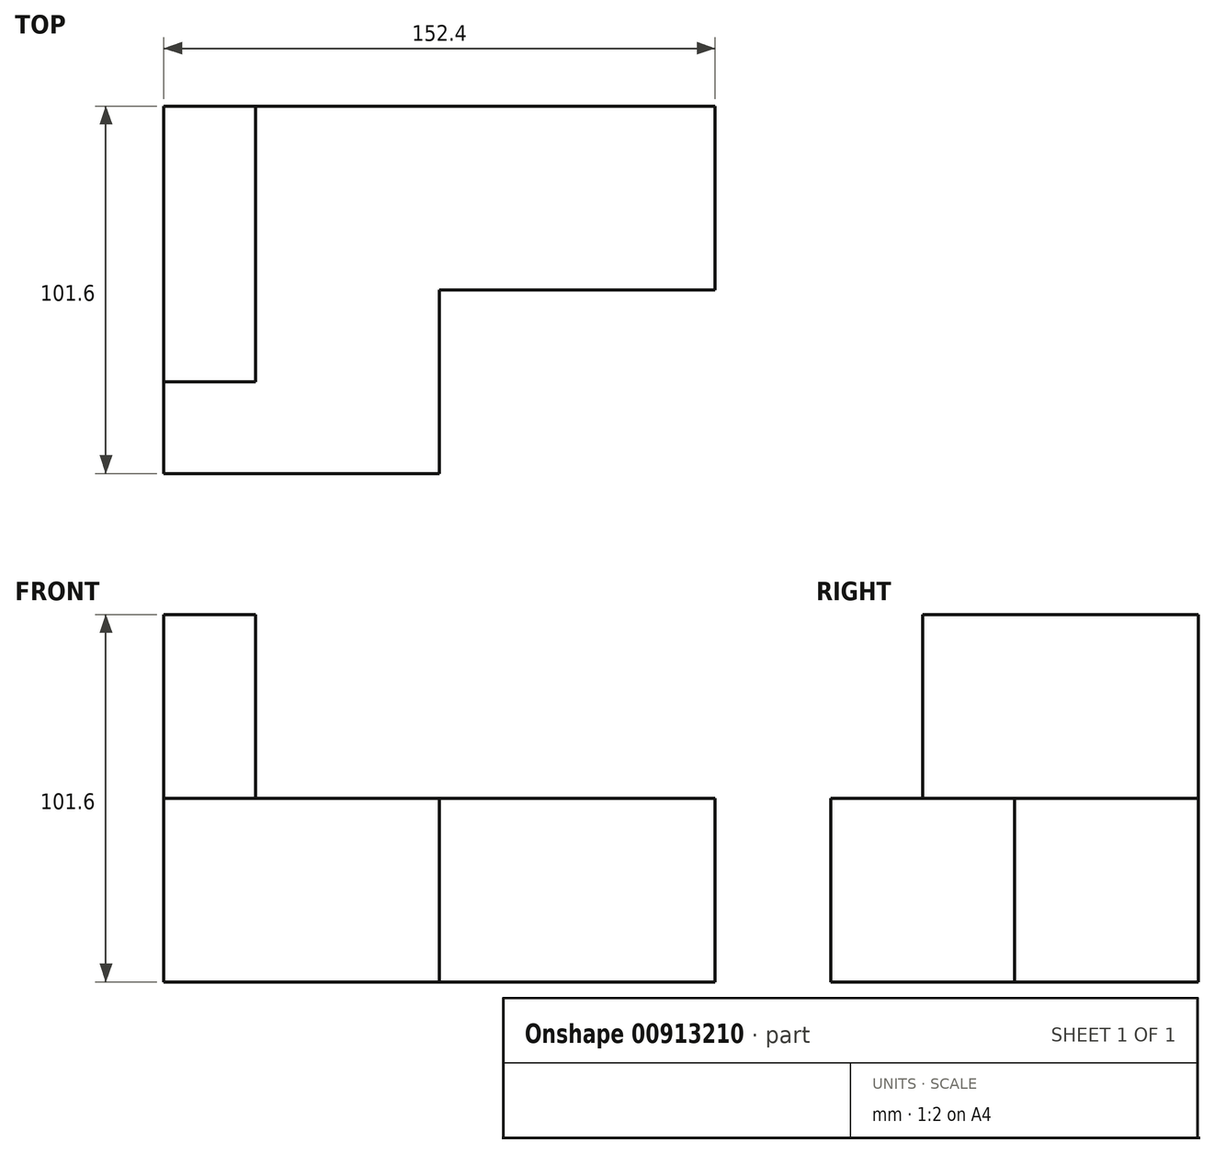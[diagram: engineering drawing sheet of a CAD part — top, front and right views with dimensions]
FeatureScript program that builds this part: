
annotation { "Feature Type Name" : "Feature", "Feature Type Description" : "" }
export const myFeature = defineFeature(function(context is Context, id is Id, definition is map)
    precondition{}
    {
        {
            var Q0;
            Q0=qCreatedBy(makeId("Top.planeOp"),FACE);
            var sketch = newSketch(context, id + "F0", { "sketchPlane" : qUnion([Q0])});
            skLineSegment(sketch, "E0.bottom", {"start": v(0, 0) * mm, "end": v(152.4, 0) * mm});
            skLineSegment(sketch, "E0.top", {"start": v(0, -101.6) * mm, "end": v(152.4, -101.6) * mm});
            skLineSegment(sketch, "E0.left", {"start": v(0, 0) * mm, "end": v(0, -101.6) * mm});
            skLineSegment(sketch, "E0.right", {"start": v(152.4, 0) * mm, "end": v(152.4, -101.6) * mm});
            skSolve(sketch);
        }
        {
            var Q0;
            Q0=makeQuery(id+"F0.imprint","IMPRINT",FACE,{"disambiguationData":[TD([[makeQuery(id+"F0.imprint","IMPRINT",EDGE,{"derivedFrom":sQuery(id+"F0.wireOp",EDGE,"E0.bottom")}),-1.0]])]});
            extrude(context, id + "F1", {"entities" : qUnion([Q0]), "depth" : 50.8 * mm, "offsetDistance" : 25.4 * mm});
        }
        {
            var Q0;
            Q0=makeQuery(id+"F1.opExtrude","CAP_FACE",FACE,{"disambiguationData":[OSD([sQuery(id+"F0.wireOp",EDGE,"E0.bottom"),sQuery(id+"F0.wireOp",EDGE,"E0.top"),sQuery(id+"F0.wireOp",EDGE,"E0.left"),sQuery(id+"F0.wireOp",EDGE,"E0.right")])],"isStart":false});
            var sketch = newSketch(context, id + "F2", { "sketchPlane" : qUnion([Q0])});
            skLineSegment(sketch, "E1.bottom", {"start": v(0, 0) * mm, "end": v(25.4, 0) * mm});
            skLineSegment(sketch, "E1.top", {"start": v(0, -76.2) * mm, "end": v(25.4, -76.2) * mm});
            skLineSegment(sketch, "E1.left", {"start": v(0, 0) * mm, "end": v(0, -76.2) * mm});
            skLineSegment(sketch, "E1.right", {"start": v(25.4, 0) * mm, "end": v(25.4, -76.2) * mm});
            skSolve(sketch);
        }
        {
            var Q0;
            Q0 = qSketchRegion(id + "F2", true);
            extrude(context, id + "F3", {"entities" : qUnion([Q0]), "operationType" : NewBodyOperationType.ADD, "depth" : 50.8 * mm, "offsetDistance" : 25.4 * mm});
        }
        {
            var Q0;
            Q0=makeQuery(id+"F1.opExtrude","CAP_FACE",FACE,{"disambiguationData":[OSD([sQuery(id+"F0.wireOp",EDGE,"E0.bottom"),sQuery(id+"F0.wireOp",EDGE,"E0.top"),sQuery(id+"F0.wireOp",EDGE,"E0.left"),sQuery(id+"F0.wireOp",EDGE,"E0.right")])],"isStart":false});
            var sketch = newSketch(context, id + "F4", { "sketchPlane" : qUnion([Q0])});
            skLineSegment(sketch, "E2.bottom", {"start": v(152.4, -101.6) * mm, "end": v(76.2, -101.6) * mm});
            skLineSegment(sketch, "E2.top", {"start": v(152.4, -50.8) * mm, "end": v(76.2, -50.8) * mm});
            skLineSegment(sketch, "E2.left", {"start": v(152.4, -101.6) * mm, "end": v(152.4, -50.8) * mm});
            skLineSegment(sketch, "E2.right", {"start": v(76.2, -101.6) * mm, "end": v(76.2, -50.8) * mm});
            skSolve(sketch);
        }
        {
            var Q0;
            Q0=makeQuery(id+"F4.imprint","IMPRINT",FACE,{"disambiguationData":[TD([[makeQuery(id+"F4.imprint","IMPRINT",EDGE,{"derivedFrom":sQuery(id+"F4.wireOp",EDGE,"E2.bottom")}),1.0]])]});
            extrude(context, id + "F5", {"entities" : qUnion([Q0]), "operationType" : NewBodyOperationType.REMOVE, "endBound" : BoundingType.THROUGH_ALL, "oppositeDirection" : true, "depth" : 25.4 * mm, "offsetDistance" : 25.4 * mm});
        }
    });
